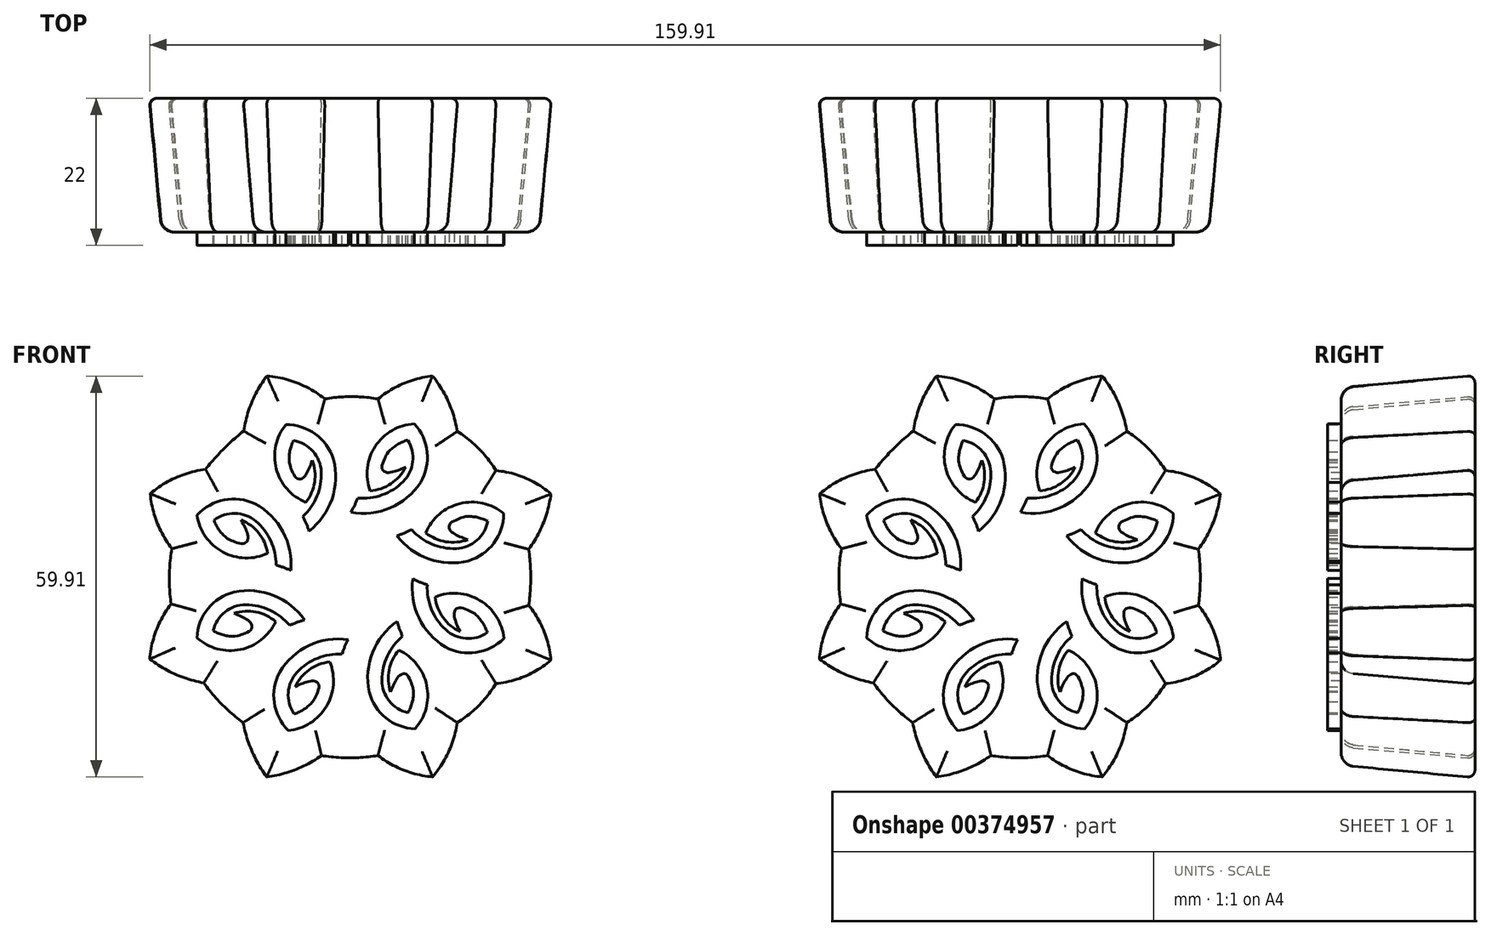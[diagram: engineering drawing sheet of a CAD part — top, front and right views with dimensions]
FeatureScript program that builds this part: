
annotation { "Feature Type Name" : "Feature", "Feature Type Description" : "" }
export const myFeature = defineFeature(function(context is Context, id is Id, definition is map)
    precondition{}
    {
        {
            var Q0;
            Q0=qCreatedBy(makeId("Front.planeOp"),FACE);
            var sketch = newSketch(context, id + "F0", { "sketchPlane" : qUnion([Q0])});
            skLineSegment(sketch, "E0", {"start": v(-48.61, 6.58) * mm, "end": v(-47.9, 5.05) * mm});
            skLineSegment(sketch, "E1", {"start": v(-47.9, 5.05) * mm, "end": v(-47.9, 5.04) * mm});
            skLineSegment(sketch, "E2", {"start": v(-47.9, 5.04) * mm, "end": v(-47, 3.58) * mm});
            skLineSegment(sketch, "E3", {"start": v(-47, 3.58) * mm, "end": v(-46.99, 3.56) * mm});
            skLineSegment(sketch, "E4", {"start": v(-46.99, 3.56) * mm, "end": v(-45.8, 1.83) * mm});
            skLineSegment(sketch, "E5", {"start": v(-45.8, 1.83) * mm, "end": v(-43.75, 2.25) * mm});
            skLineSegment(sketch, "E6", {"start": v(-43.75, 2.25) * mm, "end": v(-42.1, 2.68) * mm});
            skLineSegment(sketch, "E7", {"start": v(-42.1, 2.68) * mm, "end": v(-40.54, 3.26) * mm});
            skLineSegment(sketch, "E8", {"start": v(-40.54, 3.26) * mm, "end": v(-40.5, 3.27) * mm});
            skLineSegment(sketch, "E9", {"start": v(-40.5, 3.27) * mm, "end": v(-39.03, 4.01) * mm});
            skLineSegment(sketch, "E10", {"start": v(-39.03, 4.01) * mm, "end": v(-39, 4.03) * mm});
            skLineSegment(sketch, "E11", {"start": v(-39, 4.03) * mm, "end": v(-37.64, 4.95) * mm});
            skLineSegment(sketch, "E12", {"start": v(-37.64, 4.95) * mm, "end": v(-37.63, 4.96) * mm});
            skLineSegment(sketch, "E13", {"start": v(-37.63, 4.96) * mm, "end": v(-37.62, 4.96) * mm});
            skLineSegment(sketch, "E14", {"start": v(-37.62, 4.96) * mm, "end": v(-35.5, 4.71) * mm});
            skLineSegment(sketch, "E15", {"start": v(-35.5, 4.71) * mm, "end": v(-33.34, 4.63) * mm});
            skLineSegment(sketch, "E16", {"start": v(-33.34, 4.63) * mm, "end": v(-31.24, 4.7) * mm});
            skLineSegment(sketch, "E17", {"start": v(-31.24, 4.7) * mm, "end": v(-29.18, 4.95) * mm});
            skLineSegment(sketch, "E18", {"start": v(-29.18, 4.95) * mm, "end": v(-28.5, 4.43) * mm});
            skLineSegment(sketch, "E19", {"start": v(-28.5, 4.43) * mm, "end": v(-28.48, 4.43) * mm});
            skLineSegment(sketch, "E20", {"start": v(-28.48, 4.43) * mm, "end": v(-27.78, 3.97) * mm});
            skLineSegment(sketch, "E21", {"start": v(-27.78, 3.97) * mm, "end": v(-27.76, 3.96) * mm});
            skLineSegment(sketch, "E22", {"start": v(-27.76, 3.96) * mm, "end": v(-26.28, 3.2) * mm});
            skLineSegment(sketch, "E23", {"start": v(-26.28, 3.2) * mm, "end": v(-26.27, 3.2) * mm});
            skLineSegment(sketch, "E24", {"start": v(-26.27, 3.2) * mm, "end": v(-24.7, 2.62) * mm});
            skLineSegment(sketch, "E25", {"start": v(-24.7, 2.62) * mm, "end": v(-24.68, 2.62) * mm});
            skLineSegment(sketch, "E26", {"start": v(-24.68, 2.62) * mm, "end": v(-23.04, 2.22) * mm});
            skLineSegment(sketch, "E27", {"start": v(-23.04, 2.22) * mm, "end": v(-23, 2.22) * mm});
            skLineSegment(sketch, "E28", {"start": v(-23, 2.22) * mm, "end": v(-20.95, 1.84) * mm});
            skLineSegment(sketch, "E29", {"start": v(-20.95, 1.84) * mm, "end": v(-19.8, 3.59) * mm});
            skLineSegment(sketch, "E30", {"start": v(-19.8, 3.59) * mm, "end": v(-18.93, 5.04) * mm});
            skLineSegment(sketch, "E31", {"start": v(-18.93, 5.04) * mm, "end": v(-18.24, 6.55) * mm});
            skLineSegment(sketch, "E32", {"start": v(-18.24, 6.55) * mm, "end": v(-18.23, 6.58) * mm});
            skLineSegment(sketch, "E33", {"start": v(-18.23, 6.58) * mm, "end": v(-17.72, 8.15) * mm});
            skLineSegment(sketch, "E34", {"start": v(-17.72, 8.15) * mm, "end": v(-17.7, 8.18) * mm});
            skLineSegment(sketch, "E35", {"start": v(-17.7, 8.18) * mm, "end": v(-17.4, 9.8) * mm});
            skLineSegment(sketch, "E36", {"start": v(-17.4, 9.8) * mm, "end": v(-17.39, 9.8) * mm});
            skLineSegment(sketch, "E37", {"start": v(-17.39, 9.8) * mm, "end": v(-17.39, 9.82) * mm});
            skLineSegment(sketch, "E38", {"start": v(-17.39, 9.82) * mm, "end": v(-17.38, 9.83) * mm});
            skLineSegment(sketch, "E39", {"start": v(-17.38, 9.83) * mm, "end": v(-17.36, 9.84) * mm});
            skLineSegment(sketch, "E40", {"start": v(-17.36, 9.84) * mm, "end": v(-15.73, 11.14) * mm});
            skLineSegment(sketch, "E41", {"start": v(-15.73, 11.14) * mm, "end": v(-15.7, 11.16) * mm});
            skLineSegment(sketch, "E42", {"start": v(-15.7, 11.16) * mm, "end": v(-14.17, 12.57) * mm});
            skLineSegment(sketch, "E43", {"start": v(-14.17, 12.57) * mm, "end": v(-14.15, 12.6) * mm});
            skLineSegment(sketch, "E44", {"start": v(-14.15, 12.6) * mm, "end": v(-12.74, 14.13) * mm});
            skLineSegment(sketch, "E45", {"start": v(-12.74, 14.13) * mm, "end": v(-11.45, 15.76) * mm});
            skLineSegment(sketch, "E46", {"start": v(-11.45, 15.76) * mm, "end": v(-11.44, 15.77) * mm});
            skLineSegment(sketch, "E47", {"start": v(-11.44, 15.77) * mm, "end": v(-11.43, 15.78) * mm});
            skLineSegment(sketch, "E48", {"start": v(-11.43, 15.78) * mm, "end": v(-10.58, 15.9) * mm});
            skLineSegment(sketch, "E49", {"start": v(-10.58, 15.9) * mm, "end": v(-10.56, 15.91) * mm});
            skLineSegment(sketch, "E50", {"start": v(-10.56, 15.91) * mm, "end": v(-9.74, 16.08) * mm});
            skLineSegment(sketch, "E51", {"start": v(-9.74, 16.08) * mm, "end": v(-9.72, 16.1) * mm});
            skLineSegment(sketch, "E52", {"start": v(-9.72, 16.1) * mm, "end": v(-8.13, 16.6) * mm});
            skLineSegment(sketch, "E53", {"start": v(-8.13, 16.6) * mm, "end": v(-8.11, 16.6) * mm});
            skLineSegment(sketch, "E54", {"start": v(-8.11, 16.6) * mm, "end": v(-6.59, 17.31) * mm});
            skLineSegment(sketch, "E55", {"start": v(-6.59, 17.31) * mm, "end": v(-6.57, 17.32) * mm});
            skLineSegment(sketch, "E56", {"start": v(-6.57, 17.32) * mm, "end": v(-5.13, 18.2) * mm});
            skLineSegment(sketch, "E57", {"start": v(-5.13, 18.2) * mm, "end": v(-5.1, 18.22) * mm});
            skLineSegment(sketch, "E58", {"start": v(-5.1, 18.22) * mm, "end": v(-3.38, 19.41) * mm});
            skLineSegment(sketch, "E59", {"start": v(-3.38, 19.41) * mm, "end": v(-3.8, 21.46) * mm});
            skLineSegment(sketch, "E60", {"start": v(-3.8, 21.46) * mm, "end": v(-4.23, 23.13) * mm});
            skLineSegment(sketch, "E61", {"start": v(-4.23, 23.13) * mm, "end": v(-4.81, 24.7) * mm});
            skLineSegment(sketch, "E62", {"start": v(-4.81, 24.7) * mm, "end": v(-4.83, 24.73) * mm});
            skLineSegment(sketch, "E63", {"start": v(-4.83, 24.73) * mm, "end": v(-5.58, 26.22) * mm});
            skLineSegment(sketch, "E64", {"start": v(-5.58, 26.22) * mm, "end": v(-5.6, 26.24) * mm});
            skLineSegment(sketch, "E65", {"start": v(-5.6, 26.24) * mm, "end": v(-6.53, 27.61) * mm});
            skLineSegment(sketch, "E66", {"start": v(-6.53, 27.61) * mm, "end": v(-6.54, 27.62) * mm});
            skLineSegment(sketch, "E67", {"start": v(-6.54, 27.62) * mm, "end": v(-6.55, 27.63) * mm});
            skLineSegment(sketch, "E68", {"start": v(-6.55, 27.63) * mm, "end": v(-6.32, 29.66) * mm});
            skLineSegment(sketch, "E69", {"start": v(-6.32, 29.66) * mm, "end": v(-6.24, 31.72) * mm});
            skLineSegment(sketch, "E70", {"start": v(-6.24, 31.72) * mm, "end": v(-6.32, 33.86) * mm});
            skLineSegment(sketch, "E71", {"start": v(-6.32, 33.86) * mm, "end": v(-6.57, 35.94) * mm});
            skLineSegment(sketch, "E72", {"start": v(-6.57, 35.94) * mm, "end": v(-6.04, 36.63) * mm});
            skLineSegment(sketch, "E73", {"start": v(-6.04, 36.63) * mm, "end": v(-6.03, 36.64) * mm});
            skLineSegment(sketch, "E74", {"start": v(-6.03, 36.64) * mm, "end": v(-5.57, 37.35) * mm});
            skLineSegment(sketch, "E75", {"start": v(-5.57, 37.35) * mm, "end": v(-5.15, 38.09) * mm});
            skLineSegment(sketch, "E76", {"start": v(-5.15, 38.09) * mm, "end": v(-5.14, 38.1) * mm});
            skLineSegment(sketch, "E77", {"start": v(-5.14, 38.1) * mm, "end": v(-4.77, 38.88) * mm});
            skLineSegment(sketch, "E78", {"start": v(-4.77, 38.88) * mm, "end": v(-4.76, 38.9) * mm});
            skLineSegment(sketch, "E79", {"start": v(-4.76, 38.9) * mm, "end": v(-4.18, 40.49) * mm});
            skLineSegment(sketch, "E80", {"start": v(-4.18, 40.49) * mm, "end": v(-4.17, 40.5) * mm});
            skLineSegment(sketch, "E81", {"start": v(-4.17, 40.5) * mm, "end": v(-4.17, 40.52) * mm});
            skLineSegment(sketch, "E82", {"start": v(-4.17, 40.52) * mm, "end": v(-3.76, 42.19) * mm});
            skLineSegment(sketch, "E83", {"start": v(-3.76, 42.19) * mm, "end": v(-3.76, 42.2) * mm});
            skLineSegment(sketch, "E84", {"start": v(-3.76, 42.2) * mm, "end": v(-3.38, 44.27) * mm});
            skLineSegment(sketch, "E85", {"start": v(-3.38, 44.27) * mm, "end": v(-5.13, 45.42) * mm});
            skLineSegment(sketch, "E86", {"start": v(-5.13, 45.42) * mm, "end": v(-6.63, 46.3) * mm});
            skLineSegment(sketch, "E87", {"start": v(-6.63, 46.3) * mm, "end": v(-8.19, 47) * mm});
            skLineSegment(sketch, "E88", {"start": v(-8.19, 47) * mm, "end": v(-8.22, 47.02) * mm});
            skLineSegment(sketch, "E89", {"start": v(-8.22, 47.02) * mm, "end": v(-9.83, 47.53) * mm});
            skLineSegment(sketch, "E90", {"start": v(-9.83, 47.53) * mm, "end": v(-9.86, 47.54) * mm});
            skLineSegment(sketch, "E91", {"start": v(-9.86, 47.54) * mm, "end": v(-10.69, 47.72) * mm});
            skLineSegment(sketch, "E92", {"start": v(-10.69, 47.72) * mm, "end": v(-11.53, 47.84) * mm});
            skLineSegment(sketch, "E93", {"start": v(-11.53, 47.84) * mm, "end": v(-11.56, 47.85) * mm});
            skLineSegment(sketch, "E94", {"start": v(-11.56, 47.85) * mm, "end": v(-11.56, 47.86) * mm});
            skLineSegment(sketch, "E95", {"start": v(-11.56, 47.86) * mm, "end": v(-11.58, 47.88) * mm});
            skLineSegment(sketch, "E96", {"start": v(-11.58, 47.88) * mm, "end": v(-12.83, 49.44) * mm});
            skLineSegment(sketch, "E97", {"start": v(-12.83, 49.44) * mm, "end": v(-12.86, 49.47) * mm});
            skLineSegment(sketch, "E98", {"start": v(-12.86, 49.47) * mm, "end": v(-14.22, 50.93) * mm});
            skLineSegment(sketch, "E99", {"start": v(-14.22, 50.93) * mm, "end": v(-14.25, 50.95) * mm});
            skLineSegment(sketch, "E100", {"start": v(-14.25, 50.95) * mm, "end": v(-15.72, 52.31) * mm});
            skLineSegment(sketch, "E101", {"start": v(-15.72, 52.31) * mm, "end": v(-17.29, 53.56) * mm});
            skLineSegment(sketch, "E102", {"start": v(-17.29, 53.56) * mm, "end": v(-17.3, 53.57) * mm});
            skLineSegment(sketch, "E103", {"start": v(-17.3, 53.57) * mm, "end": v(-17.31, 53.58) * mm});
            skLineSegment(sketch, "E104", {"start": v(-17.31, 53.58) * mm, "end": v(-17.42, 54.46) * mm});
            skLineSegment(sketch, "E105", {"start": v(-17.42, 54.46) * mm, "end": v(-17.43, 54.47) * mm});
            skLineSegment(sketch, "E106", {"start": v(-17.43, 54.47) * mm, "end": v(-17.6, 55.32) * mm});
            skLineSegment(sketch, "E107", {"start": v(-17.6, 55.32) * mm, "end": v(-17.82, 56.15) * mm});
            skLineSegment(sketch, "E108", {"start": v(-17.82, 56.15) * mm, "end": v(-17.83, 56.17) * mm});
            skLineSegment(sketch, "E109", {"start": v(-17.83, 56.17) * mm, "end": v(-18.1, 56.99) * mm});
            skLineSegment(sketch, "E110", {"start": v(-18.1, 56.99) * mm, "end": v(-18.11, 57) * mm});
            skLineSegment(sketch, "E111", {"start": v(-18.11, 57) * mm, "end": v(-18.83, 58.58) * mm});
            skLineSegment(sketch, "E112", {"start": v(-18.83, 58.58) * mm, "end": v(-18.84, 58.6) * mm});
            skLineSegment(sketch, "E113", {"start": v(-18.84, 58.6) * mm, "end": v(-18.85, 58.6) * mm});
            skLineSegment(sketch, "E114", {"start": v(-18.85, 58.6) * mm, "end": v(-19.76, 60.1) * mm});
            skLineSegment(sketch, "E115", {"start": v(-19.76, 60.1) * mm, "end": v(-19.77, 60.1) * mm});
            skLineSegment(sketch, "E116", {"start": v(-19.77, 60.1) * mm, "end": v(-20.96, 61.83) * mm});
            skLineSegment(sketch, "E117", {"start": v(-20.96, 61.83) * mm, "end": v(-23.01, 61.41) * mm});
            skLineSegment(sketch, "E118", {"start": v(-23.01, 61.41) * mm, "end": v(-24.73, 60.97) * mm});
            skLineSegment(sketch, "E119", {"start": v(-24.73, 60.97) * mm, "end": v(-24.74, 60.96) * mm});
            skLineSegment(sketch, "E120", {"start": v(-24.74, 60.96) * mm, "end": v(-26.36, 60.35) * mm});
            skLineSegment(sketch, "E121", {"start": v(-26.36, 60.35) * mm, "end": v(-26.38, 60.34) * mm});
            skLineSegment(sketch, "E122", {"start": v(-26.38, 60.34) * mm, "end": v(-27.9, 59.55) * mm});
            skLineSegment(sketch, "E123", {"start": v(-27.9, 59.55) * mm, "end": v(-27.92, 59.53) * mm});
            skLineSegment(sketch, "E124", {"start": v(-27.92, 59.53) * mm, "end": v(-28.64, 59.07) * mm});
            skLineSegment(sketch, "E125", {"start": v(-28.64, 59.07) * mm, "end": v(-29.32, 58.55) * mm});
            skLineSegment(sketch, "E126", {"start": v(-29.32, 58.55) * mm, "end": v(-29.35, 58.53) * mm});
            skLineSegment(sketch, "E127", {"start": v(-29.35, 58.53) * mm, "end": v(-31.32, 58.75) * mm});
            skLineSegment(sketch, "E128", {"start": v(-31.32, 58.75) * mm, "end": v(-33.34, 58.83) * mm});
            skLineSegment(sketch, "E129", {"start": v(-33.34, 58.83) * mm, "end": v(-35.37, 58.75) * mm});
            skLineSegment(sketch, "E130", {"start": v(-35.37, 58.75) * mm, "end": v(-37.35, 58.53) * mm});
            skLineSegment(sketch, "E131", {"start": v(-37.35, 58.53) * mm, "end": v(-38.05, 59.08) * mm});
            skLineSegment(sketch, "E132", {"start": v(-38.05, 59.08) * mm, "end": v(-38.06, 59.09) * mm});
            skLineSegment(sketch, "E133", {"start": v(-38.06, 59.09) * mm, "end": v(-38.78, 59.58) * mm});
            skLineSegment(sketch, "E134", {"start": v(-38.78, 59.58) * mm, "end": v(-39.54, 60.01) * mm});
            skLineSegment(sketch, "E135", {"start": v(-39.54, 60.01) * mm, "end": v(-39.56, 60.02) * mm});
            skLineSegment(sketch, "E136", {"start": v(-39.56, 60.02) * mm, "end": v(-40.34, 60.4) * mm});
            skLineSegment(sketch, "E137", {"start": v(-40.34, 60.4) * mm, "end": v(-40.36, 60.41) * mm});
            skLineSegment(sketch, "E138", {"start": v(-40.36, 60.41) * mm, "end": v(-42, 61.02) * mm});
            skLineSegment(sketch, "E139", {"start": v(-42, 61.02) * mm, "end": v(-42, 61.03) * mm});
            skLineSegment(sketch, "E140", {"start": v(-42, 61.03) * mm, "end": v(-42.02, 61.03) * mm});
            skLineSegment(sketch, "E141", {"start": v(-42.02, 61.03) * mm, "end": v(-43.73, 61.45) * mm});
            skLineSegment(sketch, "E142", {"start": v(-43.73, 61.45) * mm, "end": v(-43.75, 61.45) * mm});
            skLineSegment(sketch, "E143", {"start": v(-43.75, 61.45) * mm, "end": v(-45.81, 61.83) * mm});
            skLineSegment(sketch, "E144", {"start": v(-45.81, 61.83) * mm, "end": v(-46.96, 60.08) * mm});
            skLineSegment(sketch, "E145", {"start": v(-46.96, 60.08) * mm, "end": v(-47.86, 58.56) * mm});
            skLineSegment(sketch, "E146", {"start": v(-47.86, 58.56) * mm, "end": v(-47.87, 58.54) * mm});
            skLineSegment(sketch, "E147", {"start": v(-47.87, 58.54) * mm, "end": v(-48.58, 56.96) * mm});
            skLineSegment(sketch, "E148", {"start": v(-48.58, 56.96) * mm, "end": v(-48.58, 56.95) * mm});
            skLineSegment(sketch, "E149", {"start": v(-48.58, 56.95) * mm, "end": v(-49.1, 55.3) * mm});
            skLineSegment(sketch, "E150", {"start": v(-49.1, 55.3) * mm, "end": v(-49.1, 55.27) * mm});
            skLineSegment(sketch, "E151", {"start": v(-49.1, 55.27) * mm, "end": v(-49.28, 54.43) * mm});
            skLineSegment(sketch, "E152", {"start": v(-49.28, 54.43) * mm, "end": v(-49.4, 53.58) * mm});
            skLineSegment(sketch, "E153", {"start": v(-49.4, 53.58) * mm, "end": v(-49.4, 53.55) * mm});
            skLineSegment(sketch, "E154", {"start": v(-49.4, 53.55) * mm, "end": v(-49.41, 53.54) * mm});
            skLineSegment(sketch, "E155", {"start": v(-49.41, 53.54) * mm, "end": v(-49.43, 53.53) * mm});
            skLineSegment(sketch, "E156", {"start": v(-49.43, 53.53) * mm, "end": v(-50.98, 52.3) * mm});
            skLineSegment(sketch, "E157", {"start": v(-50.98, 52.3) * mm, "end": v(-51, 52.27) * mm});
            skLineSegment(sketch, "E158", {"start": v(-51, 52.27) * mm, "end": v(-52.45, 50.94) * mm});
            skLineSegment(sketch, "E159", {"start": v(-52.45, 50.94) * mm, "end": v(-52.48, 50.9) * mm});
            skLineSegment(sketch, "E160", {"start": v(-52.48, 50.9) * mm, "end": v(-53.82, 49.47) * mm});
            skLineSegment(sketch, "E161", {"start": v(-53.82, 49.47) * mm, "end": v(-55.06, 47.93) * mm});
            skLineSegment(sketch, "E162", {"start": v(-55.06, 47.93) * mm, "end": v(-55.07, 47.91) * mm});
            skLineSegment(sketch, "E163", {"start": v(-55.07, 47.91) * mm, "end": v(-55.08, 47.9) * mm});
            skLineSegment(sketch, "E164", {"start": v(-55.08, 47.9) * mm, "end": v(-55.97, 47.8) * mm});
            skLineSegment(sketch, "E165", {"start": v(-55.97, 47.8) * mm, "end": v(-55.98, 47.8) * mm});
            skLineSegment(sketch, "E166", {"start": v(-55.98, 47.8) * mm, "end": v(-56.83, 47.63) * mm});
            skLineSegment(sketch, "E167", {"start": v(-56.83, 47.63) * mm, "end": v(-57.67, 47.4) * mm});
            skLineSegment(sketch, "E168", {"start": v(-57.67, 47.4) * mm, "end": v(-57.7, 47.4) * mm});
            skLineSegment(sketch, "E169", {"start": v(-57.7, 47.4) * mm, "end": v(-58.52, 47.11) * mm});
            skLineSegment(sketch, "E170", {"start": v(-58.52, 47.11) * mm, "end": v(-58.53, 47.1) * mm});
            skLineSegment(sketch, "E171", {"start": v(-58.53, 47.1) * mm, "end": v(-60.11, 46.38) * mm});
            skLineSegment(sketch, "E172", {"start": v(-60.11, 46.38) * mm, "end": v(-60.13, 46.37) * mm});
            skLineSegment(sketch, "E173", {"start": v(-60.13, 46.37) * mm, "end": v(-60.14, 46.37) * mm});
            skLineSegment(sketch, "E174", {"start": v(-60.14, 46.37) * mm, "end": v(-61.64, 45.45) * mm});
            skLineSegment(sketch, "E175", {"start": v(-61.64, 45.45) * mm, "end": v(-61.65, 45.44) * mm});
            skLineSegment(sketch, "E176", {"start": v(-61.65, 45.44) * mm, "end": v(-63.38, 44.25) * mm});
            skLineSegment(sketch, "E177", {"start": v(-63.38, 44.25) * mm, "end": v(-62.96, 42.2) * mm});
            skLineSegment(sketch, "E178", {"start": v(-62.96, 42.2) * mm, "end": v(-62.52, 40.5) * mm});
            skLineSegment(sketch, "E179", {"start": v(-62.52, 40.5) * mm, "end": v(-62.51, 40.48) * mm});
            skLineSegment(sketch, "E180", {"start": v(-62.51, 40.48) * mm, "end": v(-61.9, 38.88) * mm});
            skLineSegment(sketch, "E181", {"start": v(-61.9, 38.88) * mm, "end": v(-61.9, 38.86) * mm});
            skLineSegment(sketch, "E182", {"start": v(-61.9, 38.86) * mm, "end": v(-61.12, 37.35) * mm});
            skLineSegment(sketch, "E183", {"start": v(-61.12, 37.35) * mm, "end": v(-61.1, 37.33) * mm});
            skLineSegment(sketch, "E184", {"start": v(-61.1, 37.33) * mm, "end": v(-60.64, 36.62) * mm});
            skLineSegment(sketch, "E185", {"start": v(-60.64, 36.62) * mm, "end": v(-60.13, 35.94) * mm});
            skLineSegment(sketch, "E186", {"start": v(-60.13, 35.94) * mm, "end": v(-60.12, 35.91) * mm});
            skLineSegment(sketch, "E187", {"start": v(-60.12, 35.91) * mm, "end": v(-60.36, 33.84) * mm});
            skLineSegment(sketch, "E188", {"start": v(-60.36, 33.84) * mm, "end": v(-60.44, 31.73) * mm});
            skLineSegment(sketch, "E189", {"start": v(-60.44, 31.73) * mm, "end": v(-60.36, 29.73) * mm});
            skLineSegment(sketch, "E190", {"start": v(-60.36, 29.73) * mm, "end": v(-60.15, 27.77) * mm});
            skLineSegment(sketch, "E191", {"start": v(-60.15, 27.77) * mm, "end": v(-60.69, 27.08) * mm});
            skLineSegment(sketch, "E192", {"start": v(-60.69, 27.08) * mm, "end": v(-60.7, 27.07) * mm});
            skLineSegment(sketch, "E193", {"start": v(-60.7, 27.07) * mm, "end": v(-61.17, 26.35) * mm});
            skLineSegment(sketch, "E194", {"start": v(-61.17, 26.35) * mm, "end": v(-61.6, 25.61) * mm});
            skLineSegment(sketch, "E195", {"start": v(-61.6, 25.61) * mm, "end": v(-61.6, 25.6) * mm});
            skLineSegment(sketch, "E196", {"start": v(-61.6, 25.6) * mm, "end": v(-61.98, 24.82) * mm});
            skLineSegment(sketch, "E197", {"start": v(-61.98, 24.82) * mm, "end": v(-61.98, 24.8) * mm});
            skLineSegment(sketch, "E198", {"start": v(-61.98, 24.8) * mm, "end": v(-62.58, 23.2) * mm});
            skLineSegment(sketch, "E199", {"start": v(-62.58, 23.2) * mm, "end": v(-62.58, 23.18) * mm});
            skLineSegment(sketch, "E200", {"start": v(-62.58, 23.18) * mm, "end": v(-62.59, 23.16) * mm});
            skLineSegment(sketch, "E201", {"start": v(-62.59, 23.16) * mm, "end": v(-63, 21.48) * mm});
            skLineSegment(sketch, "E202", {"start": v(-63, 21.48) * mm, "end": v(-63, 21.47) * mm});
            skLineSegment(sketch, "E203", {"start": v(-63, 21.47) * mm, "end": v(-63.37, 19.4) * mm});
            skLineSegment(sketch, "E204", {"start": v(-63.37, 19.4) * mm, "end": v(-61.63, 18.25) * mm});
            skLineSegment(sketch, "E205", {"start": v(-61.63, 18.25) * mm, "end": v(-60.14, 17.37) * mm});
            skLineSegment(sketch, "E206", {"start": v(-60.14, 17.37) * mm, "end": v(-58.6, 16.68) * mm});
            skLineSegment(sketch, "E207", {"start": v(-58.6, 16.68) * mm, "end": v(-58.58, 16.66) * mm});
            skLineSegment(sketch, "E208", {"start": v(-58.58, 16.66) * mm, "end": v(-56.98, 16.15) * mm});
            skLineSegment(sketch, "E209", {"start": v(-56.98, 16.15) * mm, "end": v(-56.96, 16.14) * mm});
            skLineSegment(sketch, "E210", {"start": v(-56.96, 16.14) * mm, "end": v(-55.31, 15.83) * mm});
            skLineSegment(sketch, "E211", {"start": v(-55.31, 15.83) * mm, "end": v(-55.3, 15.83) * mm});
            skLineSegment(sketch, "E212", {"start": v(-55.3, 15.83) * mm, "end": v(-55.29, 15.83) * mm});
            skLineSegment(sketch, "E213", {"start": v(-55.29, 15.83) * mm, "end": v(-55.28, 15.82) * mm});
            skLineSegment(sketch, "E214", {"start": v(-55.28, 15.82) * mm, "end": v(-55.26, 15.8) * mm});
            skLineSegment(sketch, "E215", {"start": v(-55.26, 15.8) * mm, "end": v(-54, 14.19) * mm});
            skLineSegment(sketch, "E216", {"start": v(-54, 14.19) * mm, "end": v(-53.97, 14.16) * mm});
            skLineSegment(sketch, "E217", {"start": v(-53.97, 14.16) * mm, "end": v(-52.58, 12.65) * mm});
            skLineSegment(sketch, "E218", {"start": v(-52.58, 12.65) * mm, "end": v(-52.56, 12.62) * mm});
            skLineSegment(sketch, "E219", {"start": v(-52.56, 12.62) * mm, "end": v(-51.06, 11.22) * mm});
            skLineSegment(sketch, "E220", {"start": v(-51.06, 11.22) * mm, "end": v(-49.46, 9.94) * mm});
            skLineSegment(sketch, "E221", {"start": v(-49.46, 9.94) * mm, "end": v(-49.44, 9.93) * mm});
            skLineSegment(sketch, "E222", {"start": v(-49.44, 9.93) * mm, "end": v(-49.43, 9.92) * mm});
            skLineSegment(sketch, "E223", {"start": v(-49.43, 9.92) * mm, "end": v(-49.31, 9.07) * mm});
            skLineSegment(sketch, "E224", {"start": v(-49.31, 9.07) * mm, "end": v(-49.3, 9.05) * mm});
            skLineSegment(sketch, "E225", {"start": v(-49.3, 9.05) * mm, "end": v(-49.14, 8.23) * mm});
            skLineSegment(sketch, "E226", {"start": v(-49.14, 8.23) * mm, "end": v(-49.13, 8.2) * mm});
            skLineSegment(sketch, "E227", {"start": v(-49.13, 8.2) * mm, "end": v(-48.62, 6.6) * mm});
            skLineSegment(sketch, "E228", {"start": v(-48.62, 6.6) * mm, "end": v(-48.61, 6.58) * mm});
            skArc(sketch, "E229", {"start": v(1.3, 19.08) * mm, "mid": v(7.78, 17.33) * mm, "end": v(13.04, 21.5) * mm});
            skArc(sketch, "E230", {"start": v(6.84, 25.93) * mm, "mid": v(2.93, 23.43) * mm, "end": v(1.3, 19.08) * mm});
            skArc(sketch, "E231", {"start": v(17.36, 21.74) * mm, "mid": v(12.73, 25.42) * mm, "end": v(6.84, 25.93) * mm});
            skArc(sketch, "E232", {"start": v(17.36, 21.74) * mm, "mid": v(16.23, 21.4) * mm, "end": v(15.14, 20.94) * mm});
            skArc(sketch, "E233", {"start": v(15.14, 20.94) * mm, "mid": v(12.2, 23.2) * mm, "end": v(8.59, 24.02) * mm});
            skArc(sketch, "E234", {"start": v(8.59, 24.02) * mm, "mid": v(5.46, 22.93) * mm, "end": v(3.71, 20.12) * mm});
            skArc(sketch, "E235", {"start": v(3.71, 20.12) * mm, "mid": v(5.28, 19.49) * mm, "end": v(6.96, 19.31) * mm});
            skArc(sketch, "E236", {"start": v(13.04, 21.5) * mm, "mid": v(10.1, 22.95) * mm, "end": v(6.8, 22.75) * mm});
            skFitSpline(sketch, "E237", {"points": [v(6.96, 19.31) * mm, v(8.1, 19.61) * mm, v(9.2, 20.12) * mm, v(9.53, 20.68) * mm, v(9.32, 21.34) * mm, v(8.65, 21.89) * mm, v(7.89, 22.3) * mm, v(6.8, 22.75) * mm], "startDerivative": vector(11.06, 1.94) * mm, "endDerivative": vector(-7.1, 2.76) * mm});
            skPoint(sketch, "E238", {"position": v(12.01, 25.67) * mm});
            skFitSpline(sketch, "E239.MirrorCS", {"points": [v(75.38, 19.31) * mm, v(74.26, 19.61) * mm, v(73.15, 20.12) * mm, v(72.82, 20.68) * mm, v(73.02, 21.34) * mm, v(73.7, 21.89) * mm, v(74.46, 22.3) * mm, v(75.54, 22.75) * mm], "startDerivative": vector(-11.06, 1.94) * mm, "endDerivative": vector(7.1, 2.76) * mm});
            skArc(sketch, "E240.MirrorCS", {"start": v(73.76, 24.02) * mm, "mid": v(76.88, 22.93) * mm, "end": v(78.63, 20.12) * mm});
            skArc(sketch, "E241.MirrorCS", {"start": v(65, 21.74) * mm, "mid": v(66.12, 21.4) * mm, "end": v(67.2, 20.94) * mm});
            skArc(sketch, "E242.MirrorCS", {"start": v(67.2, 20.94) * mm, "mid": v(70.14, 23.2) * mm, "end": v(73.76, 24.02) * mm});
            skArc(sketch, "E243.MirrorCS", {"start": v(65, 21.74) * mm, "mid": v(69.62, 25.42) * mm, "end": v(75.51, 25.93) * mm});
            skArc(sketch, "E244.MirrorCS", {"start": v(75.51, 25.93) * mm, "mid": v(79.42, 23.43) * mm, "end": v(81.04, 19.08) * mm});
            skArc(sketch, "E245.MirrorCS", {"start": v(81.04, 19.08) * mm, "mid": v(74.56, 17.33) * mm, "end": v(69.3, 21.5) * mm});
            skPoint(sketch, "E246.MirrorP", {"position": v(70.34, 25.67) * mm});
            skArc(sketch, "E247.MirrorCS", {"start": v(78.63, 20.12) * mm, "mid": v(77.06, 19.49) * mm, "end": v(75.38, 19.31) * mm});
            skArc(sketch, "E248.MirrorCS", {"start": v(69.3, 21.5) * mm, "mid": v(72.25, 22.95) * mm, "end": v(75.54, 22.75) * mm});
            skSolve(sketch);
        }
        {
            var Q0;
            Q0=qCreatedBy(makeId("Front.planeOp"),FACE);
            var sketch = newSketch(context, id + "F1", { "sketchPlane" : qUnion([Q0])});
            skArc(sketch, "E249", {"start": v(-55.02, 47.9) * mm, "mid": v(-59.43, 46.67) * mm, "end": v(-63.32, 44.23) * mm});
            skArc(sketch, "E250", {"start": v(-63.32, 44.23) * mm, "mid": v(-62.3, 39.85) * mm, "end": v(-60.08, 35.94) * mm});
            skArc(sketch, "E251", {"start": v(-49.35, 53.6) * mm, "mid": v(-52.35, 50.92) * mm, "end": v(-55.02, 47.9) * mm});
            skArc(sketch, "E252", {"start": v(-45.86, 61.87) * mm, "mid": v(-48.11, 57.95) * mm, "end": v(-49.35, 53.6) * mm});
            skArc(sketch, "E253", {"start": v(-37.13, 58.44) * mm, "mid": v(-41.23, 60.82) * mm, "end": v(-45.86, 61.87) * mm});
            skArc(sketch, "E254", {"start": v(-29.23, 58.44) * mm, "mid": v(-33.18, 58.78) * mm, "end": v(-37.13, 58.44) * mm});
            skArc(sketch, "E255", {"start": v(-21.02, 61.87) * mm, "mid": v(-25.37, 60.75) * mm, "end": v(-29.23, 58.44) * mm});
            skArc(sketch, "E256", {"start": v(-17.29, 53.54) * mm, "mid": v(-18.61, 57.95) * mm, "end": v(-21.02, 61.87) * mm});
            skArc(sketch, "E257", {"start": v(-11.55, 47.73) * mm, "mid": v(-14.08, 50.98) * mm, "end": v(-17.29, 53.54) * mm});
            skArc(sketch, "E258", {"start": v(-3.28, 44.18) * mm, "mid": v(-7.14, 46.6) * mm, "end": v(-11.55, 47.73) * mm});
            skArc(sketch, "E259", {"start": v(-6.59, 35.85) * mm, "mid": v(-4.4, 39.8) * mm, "end": v(-3.28, 44.18) * mm});
            skArc(sketch, "E260", {"start": v(-6.59, 27.51) * mm, "mid": v(-6.3, 31.68) * mm, "end": v(-6.59, 35.85) * mm});
            skArc(sketch, "E261", {"start": v(-3.28, 19.29) * mm, "mid": v(-4.32, 23.65) * mm, "end": v(-6.59, 27.51) * mm});
            skArc(sketch, "E262", {"start": v(-11.55, 15.74) * mm, "mid": v(-7.13, 16.85) * mm, "end": v(-3.28, 19.29) * mm});
            skArc(sketch, "E263", {"start": v(-17.29, 9.92) * mm, "mid": v(-14.07, 12.49) * mm, "end": v(-11.55, 15.74) * mm});
            skArc(sketch, "E264", {"start": v(-21.02, 1.76) * mm, "mid": v(-18.58, 5.58) * mm, "end": v(-17.29, 9.92) * mm});
            skArc(sketch, "E265", {"start": v(-29.23, 4.97) * mm, "mid": v(-25.36, 2.78) * mm, "end": v(-21.02, 1.76) * mm});
            skArc(sketch, "E266", {"start": v(-37.63, 4.97) * mm, "mid": v(-33.43, 4.62) * mm, "end": v(-29.23, 4.97) * mm});
            skArc(sketch, "E267", {"start": v(-45.86, 1.76) * mm, "mid": v(-41.54, 2.86) * mm, "end": v(-37.63, 4.97) * mm});
            skArc(sketch, "E268", {"start": v(-49.43, 9.92) * mm, "mid": v(-48.1, 5.64) * mm, "end": v(-45.86, 1.76) * mm});
            skArc(sketch, "E269", {"start": v(-55.27, 15.83) * mm, "mid": v(-52.59, 12.65) * mm, "end": v(-49.43, 9.92) * mm});
            skArc(sketch, "E270", {"start": v(-63.39, 19.42) * mm, "mid": v(-59.54, 17.14) * mm, "end": v(-55.27, 15.83) * mm});
            skArc(sketch, "E271", {"start": v(-60.2, 27.73) * mm, "mid": v(-62.4, 23.8) * mm, "end": v(-63.39, 19.42) * mm});
            skArc(sketch, "E272", {"start": v(-60.08, 35.94) * mm, "mid": v(-60.46, 31.84) * mm, "end": v(-60.2, 27.73) * mm});
            skSolve(sketch);
        }
        {
            var Q0;
            Q0=makeQuery(id+"F1.imprint","IMPRINT",FACE,{"disambiguationData":[TD([[makeQuery(id+"F1.imprint","IMPRINT",EDGE,{"derivedFrom":sQuery(id+"F1.wireOp",EDGE,"E249")}),1.0]])]});
            extrude(context, id + "F2", {"entities" : qUnion([Q0]), "depth" : 20 * mm, "hasDraft" : true, "draftAngle" : 5 * degree, "draftPullDirection" : true});
        }
        {
            var Q0;
            Q0=makeQuery(id+"F2.opExtrude","CAP_FACE",FACE,{"disambiguationData":[OSD([sQuery(id+"F1.wireOp",EDGE,"E249"),sQuery(id+"F1.wireOp",EDGE,"E250"),sQuery(id+"F1.wireOp",EDGE,"E251"),sQuery(id+"F1.wireOp",EDGE,"E252"),sQuery(id+"F1.wireOp",EDGE,"E253"),sQuery(id+"F1.wireOp",EDGE,"E254"),sQuery(id+"F1.wireOp",EDGE,"E255"),sQuery(id+"F1.wireOp",EDGE,"E256"),sQuery(id+"F1.wireOp",EDGE,"E257"),sQuery(id+"F1.wireOp",EDGE,"E258"),sQuery(id+"F1.wireOp",EDGE,"E259"),sQuery(id+"F1.wireOp",EDGE,"E260"),sQuery(id+"F1.wireOp",EDGE,"E261"),sQuery(id+"F1.wireOp",EDGE,"E262"),sQuery(id+"F1.wireOp",EDGE,"E263"),sQuery(id+"F1.wireOp",EDGE,"E264"),sQuery(id+"F1.wireOp",EDGE,"E265"),sQuery(id+"F1.wireOp",EDGE,"E266"),sQuery(id+"F1.wireOp",EDGE,"E267"),sQuery(id+"F1.wireOp",EDGE,"E268"),sQuery(id+"F1.wireOp",EDGE,"E269"),sQuery(id+"F1.wireOp",EDGE,"E270"),sQuery(id+"F1.wireOp",EDGE,"E271"),sQuery(id+"F1.wireOp",EDGE,"E272")])],"isStart":false});
            fillet(context, id + "F3", {"entities" : qUnion([Q0]), "radius" : 2 * mm, "tangentPropagation" : true, "allowEdgeOverflow" : false});
        }
        {
            var Q0;
            Q0=makeQuery(id+"F0.imprint","IMPRINT",FACE,{"disambiguationData":[TD([[makeQuery(id+"F0.imprint","IMPRINT",EDGE,{"derivedFrom":sQuery(id+"F0.wireOp",EDGE,"E229")}),1.0]])]});
            var sketch = newSketch(context, id + "F4", { "sketchPlane" : qUnion([Q0])});
            skArc(sketch, "E273", {"start": v(-56.23, 22.64) * mm, "mid": v(-49.76, 20.9) * mm, "end": v(-44.5, 25.06) * mm});
            skArc(sketch, "E274", {"start": v(-50.7, 29.5) * mm, "mid": v(-54.6, 27) * mm, "end": v(-56.23, 22.64) * mm});
            skArc(sketch, "E275", {"start": v(-40.18, 25.3) * mm, "mid": v(-44.81, 28.98) * mm, "end": v(-50.7, 29.5) * mm});
            skArc(sketch, "E276", {"start": v(-40.18, 25.3) * mm, "mid": v(-41.3, 24.96) * mm, "end": v(-42.4, 24.5) * mm});
            skArc(sketch, "E277", {"start": v(-42.4, 24.5) * mm, "mid": v(-45.33, 26.77) * mm, "end": v(-48.95, 27.58) * mm});
            skArc(sketch, "E278", {"start": v(-48.95, 27.58) * mm, "mid": v(-52.07, 26.5) * mm, "end": v(-53.82, 23.68) * mm});
            skArc(sketch, "E279", {"start": v(-53.82, 23.68) * mm, "mid": v(-52.26, 23.05) * mm, "end": v(-50.57, 22.87) * mm});
            skArc(sketch, "E280", {"start": v(-44.5, 25.06) * mm, "mid": v(-47.44, 26.51) * mm, "end": v(-50.73, 26.32) * mm});
            skFitSpline(sketch, "E281", {"points": [v(-50.57, 22.87) * mm, v(-49.45, 23.18) * mm, v(-48.34, 23.69) * mm, v(-48.01, 24.24) * mm, v(-48.21, 24.9) * mm, v(-48.88, 25.45) * mm, v(-49.65, 25.87) * mm, v(-50.73, 26.32) * mm], "startDerivative": vector(11.06, 1.94) * mm, "endDerivative": vector(-7.1, 2.76) * mm});
            skArc(sketch, "E282", {"start": v(-42.61, 8.8) * mm, "mid": v(-36.93, 12.36) * mm, "end": v(-36.4, 19.06) * mm});
            skArc(sketch, "E283", {"start": v(-43.88, 17.52) * mm, "mid": v(-44.7, 12.95) * mm, "end": v(-42.61, 8.8) * mm});
            skArc(sketch, "E284", {"start": v(-33.66, 22.39) * mm, "mid": v(-39.5, 21.5) * mm, "end": v(-43.88, 17.52) * mm});
            skArc(sketch, "E285", {"start": v(-33.66, 22.39) * mm, "mid": v(-34.17, 21.33) * mm, "end": v(-34.57, 20.22) * mm});
            skArc(sketch, "E286", {"start": v(-34.57, 20.22) * mm, "mid": v(-38.23, 19.6) * mm, "end": v(-41.29, 17.5) * mm});
            skArc(sketch, "E287", {"start": v(-41.29, 17.5) * mm, "mid": v(-42.6, 14.47) * mm, "end": v(-41.74, 11.28) * mm});
            skArc(sketch, "E288", {"start": v(-41.74, 11.28) * mm, "mid": v(-40.2, 12) * mm, "end": v(-38.94, 13.11) * mm});
            skArc(sketch, "E289", {"start": v(-36.4, 19.06) * mm, "mid": v(-39.48, 17.88) * mm, "end": v(-41.57, 15.34) * mm});
            skFitSpline(sketch, "E290", {"points": [v(-38.94, 13.11) * mm, v(-38.4, 14.14) * mm, v(-38.02, 15.3) * mm, v(-38.2, 15.92) * mm, v(-38.82, 16.22) * mm, v(-39.68, 16.1) * mm, v(-40.51, 15.83) * mm, v(-41.57, 15.34) * mm], "startDerivative": vector(6.1, 9.43) * mm, "endDerivative": vector(-6.85, -3.33) * mm});
            skArc(sketch, "E291", {"start": v(-56.22, 40.98) * mm, "mid": v(-52.38, 35.47) * mm, "end": v(-45.67, 35.28) * mm});
            skArc(sketch, "E292", {"start": v(-47.57, 42.67) * mm, "mid": v(-52.18, 43.26) * mm, "end": v(-56.22, 40.98) * mm});
            skArc(sketch, "E293", {"start": v(-42.2, 32.7) * mm, "mid": v(-43.4, 38.49) * mm, "end": v(-47.57, 42.67) * mm});
            skArc(sketch, "E294", {"start": v(-42.2, 32.7) * mm, "mid": v(-43.3, 33.16) * mm, "end": v(-44.42, 33.5) * mm});
            skArc(sketch, "E295", {"start": v(-44.42, 33.5) * mm, "mid": v(-45.2, 37.13) * mm, "end": v(-47.46, 40.08) * mm});
            skArc(sketch, "E296", {"start": v(-47.46, 40.08) * mm, "mid": v(-50.56, 41.25) * mm, "end": v(-53.7, 40.22) * mm});
            skArc(sketch, "E297", {"start": v(-53.7, 40.22) * mm, "mid": v(-52.9, 38.73) * mm, "end": v(-51.73, 37.51) * mm});
            skArc(sketch, "E298", {"start": v(-45.67, 35.28) * mm, "mid": v(-47, 38.29) * mm, "end": v(-49.64, 40.25) * mm});
            skFitSpline(sketch, "E299", {"points": [v(-51.73, 37.51) * mm, v(-50.67, 37.02) * mm, v(-49.5, 36.7) * mm, v(-48.9, 36.91) * mm, v(-48.62, 37.55) * mm, v(-48.78, 38.4) * mm, v(-49.1, 39.22) * mm, v(-49.64, 40.25) * mm], "startDerivative": vector(9.72, -5.62) * mm, "endDerivative": vector(-3.66, 6.67) * mm});
            skArc(sketch, "E300", {"start": v(-10.44, 41.22) * mm, "mid": v(-16.98, 42.7) * mm, "end": v(-22.07, 38.33) * mm});
            skArc(sketch, "E301", {"start": v(-15.7, 34.15) * mm, "mid": v(-11.89, 36.8) * mm, "end": v(-10.44, 41.22) * mm});
            skArc(sketch, "E302", {"start": v(-26.37, 37.91) * mm, "mid": v(-21.6, 34.42) * mm, "end": v(-15.7, 34.15) * mm});
            skArc(sketch, "E303", {"start": v(-26.37, 37.91) * mm, "mid": v(-25.26, 38.3) * mm, "end": v(-24.2, 38.8) * mm});
            skArc(sketch, "E304", {"start": v(-24.2, 38.8) * mm, "mid": v(-21.17, 36.66) * mm, "end": v(-17.52, 35.99) * mm});
            skArc(sketch, "E305", {"start": v(-17.52, 35.99) * mm, "mid": v(-14.44, 37.2) * mm, "end": v(-12.8, 40.08) * mm});
            skArc(sketch, "E306", {"start": v(-12.8, 40.08) * mm, "mid": v(-14.4, 40.65) * mm, "end": v(-16.09, 40.76) * mm});
            skArc(sketch, "E307", {"start": v(-22.07, 38.33) * mm, "mid": v(-19.07, 37) * mm, "end": v(-15.8, 37.33) * mm});
            skFitSpline(sketch, "E308", {"points": [v(-16.09, 40.76) * mm, v(-17.2, 40.41) * mm, v(-18.28, 39.86) * mm, v(-18.6, 39.3) * mm, v(-18.36, 38.64) * mm, v(-17.67, 38.12) * mm, v(-16.89, 37.73) * mm, v(-15.8, 37.33) * mm], "startDerivative": vector(-10.97, -2.38) * mm, "endDerivative": vector(7.2, -2.47) * mm});
            skArc(sketch, "E309", {"start": v(-23.79, 54.62) * mm, "mid": v(-29.6, 51.28) * mm, "end": v(-30.38, 44.61) * mm});
            skArc(sketch, "E310", {"start": v(-22.85, 45.86) * mm, "mid": v(-21.86, 50.4) * mm, "end": v(-23.79, 54.62) * mm});
            skArc(sketch, "E311", {"start": v(-33.26, 41.4) * mm, "mid": v(-27.38, 42.06) * mm, "end": v(-22.85, 45.86) * mm});
            skArc(sketch, "E312", {"start": v(-33.26, 41.4) * mm, "mid": v(-32.7, 42.43) * mm, "end": v(-32.26, 43.52) * mm});
            skArc(sketch, "E313", {"start": v(-32.26, 43.52) * mm, "mid": v(-28.58, 44) * mm, "end": v(-25.45, 45.98) * mm});
            skArc(sketch, "E314", {"start": v(-25.45, 45.98) * mm, "mid": v(-24, 48.96) * mm, "end": v(-24.76, 52.18) * mm});
            skArc(sketch, "E315", {"start": v(-24.76, 52.18) * mm, "mid": v(-26.31, 51.52) * mm, "end": v(-27.63, 50.46) * mm});
            skArc(sketch, "E316", {"start": v(-30.38, 44.61) * mm, "mid": v(-27.27, 45.67) * mm, "end": v(-25.08, 48.13) * mm});
            skFitSpline(sketch, "E317", {"points": [v(-27.63, 50.46) * mm, v(-28.2, 49.45) * mm, v(-28.63, 48.3) * mm, v(-28.47, 47.68) * mm, v(-27.87, 47.36) * mm, v(-27, 47.44) * mm, v(-26.16, 47.69) * mm, v(-25.08, 48.13) * mm], "startDerivative": vector(-6.45, -9.2) * mm, "endDerivative": vector(6.97, 3.07) * mm});
            skArc(sketch, "E318", {"start": v(-42.98, 54.5) * mm, "mid": v(-44.4, 47.94) * mm, "end": v(-39.97, 42.9) * mm});
            skArc(sketch, "E319", {"start": v(-35.85, 49.31) * mm, "mid": v(-38.55, 53.09) * mm, "end": v(-42.98, 54.5) * mm});
            skArc(sketch, "E320", {"start": v(-39.51, 38.6) * mm, "mid": v(-36.07, 43.4) * mm, "end": v(-35.85, 49.31) * mm});
            skArc(sketch, "E321", {"start": v(-39.51, 38.6) * mm, "mid": v(-39.9, 39.7) * mm, "end": v(-40.42, 40.76) * mm});
            skArc(sketch, "E322", {"start": v(-40.42, 40.76) * mm, "mid": v(-38.3, 43.81) * mm, "end": v(-37.68, 47.47) * mm});
            skArc(sketch, "E323", {"start": v(-37.68, 47.47) * mm, "mid": v(-38.92, 50.53) * mm, "end": v(-41.82, 52.14) * mm});
            skArc(sketch, "E324", {"start": v(-41.82, 52.14) * mm, "mid": v(-42.37, 50.54) * mm, "end": v(-42.46, 48.85) * mm});
            skArc(sketch, "E325", {"start": v(-39.97, 42.9) * mm, "mid": v(-38.67, 45.91) * mm, "end": v(-39.03, 49.18) * mm});
            skFitSpline(sketch, "E326", {"points": [v(-42.46, 48.85) * mm, v(-42.1, 47.74) * mm, v(-41.54, 46.67) * mm, v(-40.97, 46.36) * mm, v(-40.32, 46.6) * mm, v(-39.8, 47.3) * mm, v(-39.42, 48.08) * mm, v(-39.03, 49.18) * mm], "startDerivative": vector(2.5, -10.95) * mm, "endDerivative": vector(2.4, 7.22) * mm});
            skArc(sketch, "E327", {"start": v(-23.68, 9.05) * mm, "mid": v(-21.93, 15.53) * mm, "end": v(-26.1, 20.79) * mm});
            skArc(sketch, "E328", {"start": v(-30.53, 14.58) * mm, "mid": v(-28.02, 10.68) * mm, "end": v(-23.68, 9.05) * mm});
            skArc(sketch, "E329", {"start": v(-26.34, 25.1) * mm, "mid": v(-30.02, 20.47) * mm, "end": v(-30.53, 14.58) * mm});
            skArc(sketch, "E330", {"start": v(-26.34, 25.1) * mm, "mid": v(-26, 23.97) * mm, "end": v(-25.54, 22.9) * mm});
            skArc(sketch, "E331", {"start": v(-25.54, 22.9) * mm, "mid": v(-27.8, 19.95) * mm, "end": v(-28.62, 16.33) * mm});
            skArc(sketch, "E332", {"start": v(-28.62, 16.33) * mm, "mid": v(-27.52, 13.21) * mm, "end": v(-24.72, 11.46) * mm});
            skArc(sketch, "E333", {"start": v(-24.72, 11.46) * mm, "mid": v(-24.08, 13.03) * mm, "end": v(-23.9, 14.71) * mm});
            skArc(sketch, "E334", {"start": v(-26.1, 20.79) * mm, "mid": v(-27.55, 17.84) * mm, "end": v(-27.35, 14.55) * mm});
            skFitSpline(sketch, "E335", {"points": [v(-23.9, 14.71) * mm, v(-24.21, 15.84) * mm, v(-24.72, 16.94) * mm, v(-25.27, 17.27) * mm, v(-25.93, 17.07) * mm, v(-26.48, 16.4) * mm, v(-26.9, 15.63) * mm, v(-27.35, 14.55) * mm], "startDerivative": vector(-1.94, 11.06) * mm, "endDerivative": vector(-2.76, -7.1) * mm});
            skArc(sketch, "E336", {"start": v(-10.4, 22.56) * mm, "mid": v(-13.98, 28.24) * mm, "end": v(-20.67, 28.74) * mm});
            skArc(sketch, "E337", {"start": v(-19.12, 21.27) * mm, "mid": v(-14.55, 20.46) * mm, "end": v(-10.4, 22.56) * mm});
            skArc(sketch, "E338", {"start": v(-24, 31.49) * mm, "mid": v(-23.1, 25.65) * mm, "end": v(-19.12, 21.27) * mm});
            skArc(sketch, "E339", {"start": v(-24, 31.49) * mm, "mid": v(-22.95, 30.98) * mm, "end": v(-21.84, 30.58) * mm});
            skArc(sketch, "E340", {"start": v(-21.84, 30.58) * mm, "mid": v(-21.22, 26.92) * mm, "end": v(-19.11, 23.87) * mm});
            skArc(sketch, "E341", {"start": v(-19.11, 23.87) * mm, "mid": v(-16.08, 22.55) * mm, "end": v(-12.88, 23.43) * mm});
            skArc(sketch, "E342", {"start": v(-12.88, 23.43) * mm, "mid": v(-13.6, 24.96) * mm, "end": v(-14.73, 26.23) * mm});
            skArc(sketch, "E343", {"start": v(-20.67, 28.74) * mm, "mid": v(-19.5, 25.67) * mm, "end": v(-16.95, 23.6) * mm});
            skFitSpline(sketch, "E344", {"points": [v(-14.73, 26.23) * mm, v(-15.76, 26.77) * mm, v(-16.91, 27.14) * mm, v(-17.53, 26.96) * mm, v(-17.83, 26.34) * mm, v(-17.71, 25.48) * mm, v(-17.44, 24.65) * mm, v(-16.95, 23.6) * mm], "startDerivative": vector(-9.44, 6.07) * mm, "endDerivative": vector(3.34, -6.84) * mm});
            skSolve(sketch);
        }
        {
            var Q0;
            Q0=makeQuery(id+"F4.imprint","IMPRINT",FACE,{"disambiguationData":[TD([[makeQuery(id+"F4.imprint","IMPRINT",EDGE,{"derivedFrom":sQuery(id+"F4.wireOp",EDGE,"E309")}),1.0]])]});
            var Q1;
            Q1=makeQuery(id+"F4.imprint","IMPRINT",FACE,{"disambiguationData":[TD([[makeQuery(id+"F4.imprint","IMPRINT",EDGE,{"derivedFrom":sQuery(id+"F4.wireOp",EDGE,"E300")}),1.0]])]});
            var Q2;
            Q2=makeQuery(id+"F4.imprint","IMPRINT",FACE,{"disambiguationData":[TD([[makeQuery(id+"F4.imprint","IMPRINT",EDGE,{"derivedFrom":sQuery(id+"F4.wireOp",EDGE,"E336")}),1.0]])]});
            var Q3;
            Q3=makeQuery(id+"F4.imprint","IMPRINT",FACE,{"disambiguationData":[TD([[makeQuery(id+"F4.imprint","IMPRINT",EDGE,{"derivedFrom":sQuery(id+"F4.wireOp",EDGE,"E327")}),1.0]])]});
            var Q4;
            Q4=makeQuery(id+"F4.imprint","IMPRINT",FACE,{"disambiguationData":[TD([[makeQuery(id+"F4.imprint","IMPRINT",EDGE,{"derivedFrom":sQuery(id+"F4.wireOp",EDGE,"E282")}),1.0]])]});
            var Q5;
            Q5=makeQuery(id+"F4.imprint","IMPRINT",FACE,{"disambiguationData":[TD([[makeQuery(id+"F4.imprint","IMPRINT",EDGE,{"derivedFrom":sQuery(id+"F4.wireOp",EDGE,"E273")}),1.0]])]});
            var Q6;
            Q6=makeQuery(id+"F4.imprint","IMPRINT",FACE,{"disambiguationData":[TD([[makeQuery(id+"F4.imprint","IMPRINT",EDGE,{"derivedFrom":sQuery(id+"F4.wireOp",EDGE,"E291")}),1.0]])]});
            var Q7;
            Q7=makeQuery(id+"F4.imprint","IMPRINT",FACE,{"disambiguationData":[TD([[makeQuery(id+"F4.imprint","IMPRINT",EDGE,{"derivedFrom":sQuery(id+"F4.wireOp",EDGE,"E318")}),1.0]])]});
            extrude(context, id + "F5", {"entities" : qUnion([Q0, Q1, Q2, Q3, Q4, Q5, Q6, Q7]), "operationType" : NewBodyOperationType.ADD, "depth" : 22 * mm});
        }
        {
            var Q0;
            Q0=makeQuery(id+"F2.opExtrude","CAP_FACE",FACE,{"disambiguationData":[OSD([sQuery(id+"F1.wireOp",EDGE,"E249"),sQuery(id+"F1.wireOp",EDGE,"E250"),sQuery(id+"F1.wireOp",EDGE,"E251"),sQuery(id+"F1.wireOp",EDGE,"E252"),sQuery(id+"F1.wireOp",EDGE,"E253"),sQuery(id+"F1.wireOp",EDGE,"E254"),sQuery(id+"F1.wireOp",EDGE,"E255"),sQuery(id+"F1.wireOp",EDGE,"E256"),sQuery(id+"F1.wireOp",EDGE,"E257"),sQuery(id+"F1.wireOp",EDGE,"E258"),sQuery(id+"F1.wireOp",EDGE,"E259"),sQuery(id+"F1.wireOp",EDGE,"E260"),sQuery(id+"F1.wireOp",EDGE,"E261"),sQuery(id+"F1.wireOp",EDGE,"E262"),sQuery(id+"F1.wireOp",EDGE,"E263"),sQuery(id+"F1.wireOp",EDGE,"E264"),sQuery(id+"F1.wireOp",EDGE,"E265"),sQuery(id+"F1.wireOp",EDGE,"E266"),sQuery(id+"F1.wireOp",EDGE,"E267"),sQuery(id+"F1.wireOp",EDGE,"E268"),sQuery(id+"F1.wireOp",EDGE,"E269"),sQuery(id+"F1.wireOp",EDGE,"E270"),sQuery(id+"F1.wireOp",EDGE,"E271"),sQuery(id+"F1.wireOp",EDGE,"E272")])],"isStart":true});
            fillet(context, id + "F6", {"entities" : qUnion([Q0]), "radius" : 1 * mm, "tangentPropagation" : true, "allowEdgeOverflow" : false});
        }
        {
            var Q0;
            Q0=makeQuery(id+"F2.opExtrude","SWEPT_BODY",BODY,{"disambiguationData":[OSD([sQuery(id+"F1.wireOp",EDGE,"E249"),sQuery(id+"F1.wireOp",EDGE,"E250"),sQuery(id+"F1.wireOp",EDGE,"E251"),sQuery(id+"F1.wireOp",EDGE,"E252"),sQuery(id+"F1.wireOp",EDGE,"E253"),sQuery(id+"F1.wireOp",EDGE,"E254"),sQuery(id+"F1.wireOp",EDGE,"E255"),sQuery(id+"F1.wireOp",EDGE,"E256"),sQuery(id+"F1.wireOp",EDGE,"E257"),sQuery(id+"F1.wireOp",EDGE,"E258"),sQuery(id+"F1.wireOp",EDGE,"E259"),sQuery(id+"F1.wireOp",EDGE,"E260"),sQuery(id+"F1.wireOp",EDGE,"E261"),sQuery(id+"F1.wireOp",EDGE,"E262"),sQuery(id+"F1.wireOp",EDGE,"E263"),sQuery(id+"F1.wireOp",EDGE,"E264"),sQuery(id+"F1.wireOp",EDGE,"E265"),sQuery(id+"F1.wireOp",EDGE,"E266"),sQuery(id+"F1.wireOp",EDGE,"E267"),sQuery(id+"F1.wireOp",EDGE,"E268"),sQuery(id+"F1.wireOp",EDGE,"E269"),sQuery(id+"F1.wireOp",EDGE,"E270"),sQuery(id+"F1.wireOp",EDGE,"E271"),sQuery(id+"F1.wireOp",EDGE,"E272")])]});
            transform(context, id + "F7", {"entities" : qUnion([Q0]), "transformType" : TransformType.TRANSLATION_3D, "dx" : 100 * mm, "dy" : 0 * mm, "dz" : 0 * mm, "makeCopy" : true});
        }
    });
